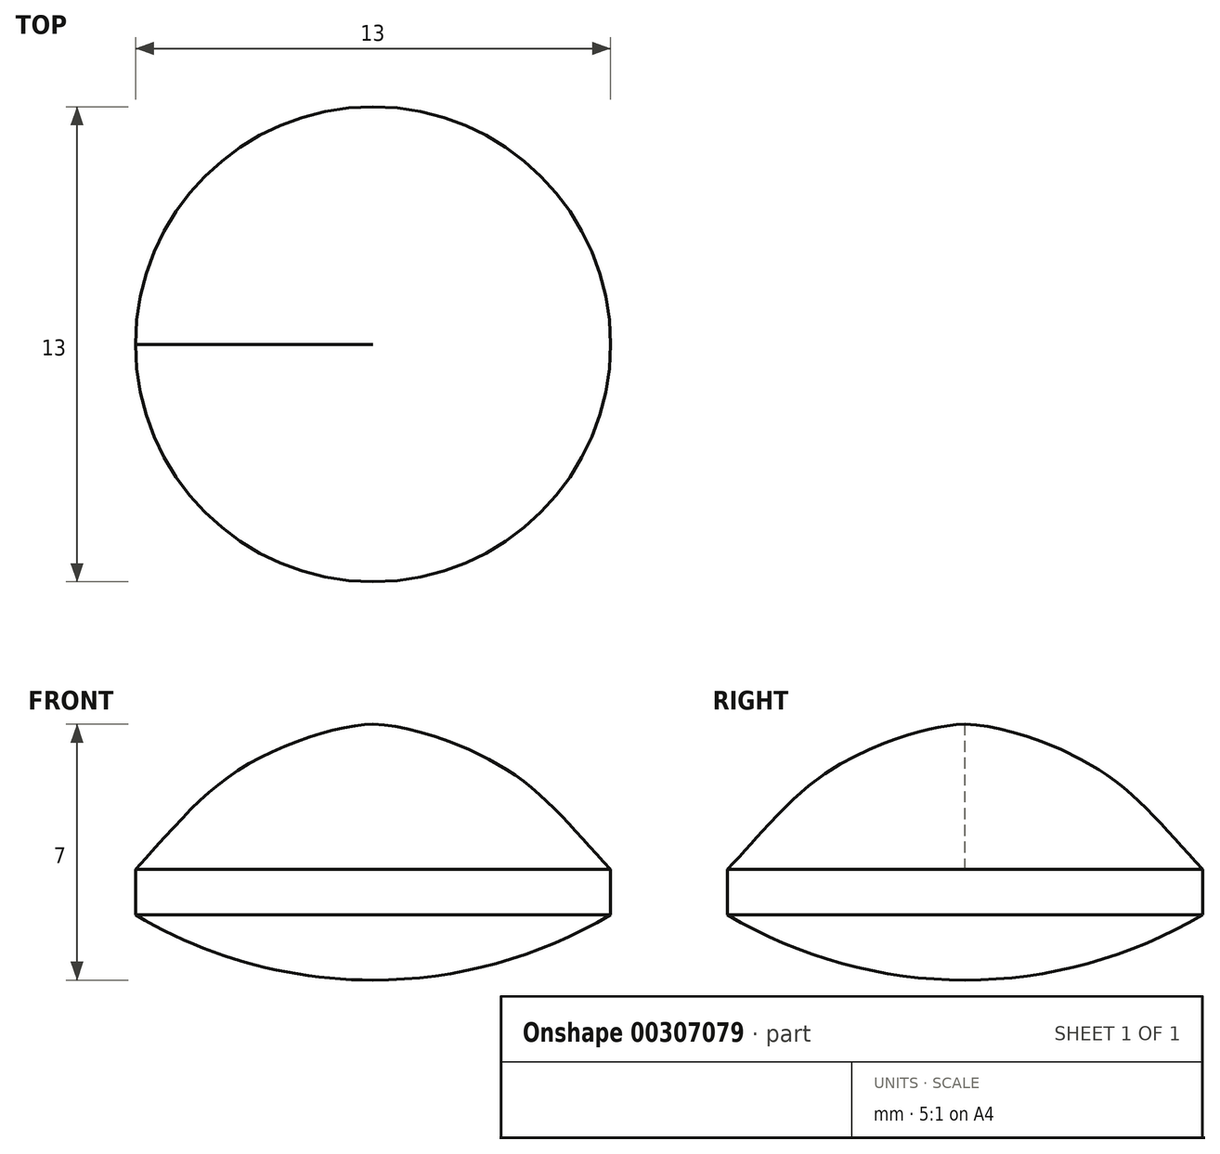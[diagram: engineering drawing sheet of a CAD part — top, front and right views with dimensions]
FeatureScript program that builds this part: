
annotation { "Feature Type Name" : "Feature", "Feature Type Description" : "" }
export const myFeature = defineFeature(function(context is Context, id is Id, definition is map)
    precondition{}
    {
        {
            var Q0;
            Q0=qCreatedBy(makeId("Front.planeOp"),FACE);
            var sketch = newSketch(context, id + "F0", { "sketchPlane" : qUnion([Q0])});
            skArc(sketch, "E0", {"start": v(-6.5, 1.79) * mm, "mid": v(-3.37, 0.45) * mm, "end": v(0, 0) * mm});
            skLineSegment(sketch, "E1", {"start": v(0, 23.83) * mm, "end": v(0, -8.8) * mm, "construction": true});
            skLineSegment(sketch, "E2", {"start": v(-6.5, 1.79) * mm, "end": v(-6.5, 3.03) * mm});
            skLineSegment(sketch, "E3", {"start": v(-6.5, 3.03) * mm, "end": v(0, 3.03) * mm});
            skFitSpline(sketch, "E4", {"points": [v(-6.5, 3.03) * mm, v(-3.4, 5.92) * mm, v(0, 7) * mm], "startDerivative": vector(6.57, 7.17) * mm, "endDerivative": vector(5.02, 0) * mm});
            skLineSegment(sketch, "E5", {"start": v(-6.5, 1.79) * mm, "end": v(0, 1.79) * mm});
            skArc(sketch, "E6", {"start": v(0, 7) * mm, "mid": v(-1.6, 6.34) * mm, "end": v(-2.27, 4.73) * mm, "construction": true});
            skLineSegment(sketch, "E7", {"start": v(0, 4.73) * mm, "end": v(-2.27, 4.73) * mm, "construction": true});
            skLineSegment(sketch, "E8", {"start": v(0, 7) * mm, "end": v(-1.08, 7) * mm, "construction": true});
            skLineSegment(sketch, "E9", {"start": v(0, 7) * mm, "end": v(0, 0) * mm});
            skSolve(sketch);
        }
        {
            var Q0;
            {var subQ0=sQuery(id+"F0.wireOp",EDGE,"E0");Q0=makeQuery(id+"F0.imprint","IMPRINT",FACE,{"disambiguationData":[TD([[makeQuery(id+"F0.imprint","IMPRINT",EDGE,{"derivedFrom":subQ0}),1.0]])]});}
            var Q1;
            Q1=makeQuery(id+"F0.imprint","IMPRINT",FACE,{"disambiguationData":[TD([[makeQuery(id+"F0.imprint","IMPRINT",EDGE,{"derivedFrom":sQuery(id+"F0.wireOp",EDGE,"E2")}),-1.0]])]});
            var Q2;
            {var subQ0=sQuery(id+"F0.wireOp",EDGE,"E3");Q2=makeQuery(id+"F0.imprint","IMPRINT",FACE,{"disambiguationData":[TD([[makeQuery(id+"F0.imprint","IMPRINT",EDGE,{"derivedFrom":subQ0}),1.0]])]});}
            var Q3;
            Q3=sQuery(id+"F0.wireOp",EDGE,"E9");
            revolve(context, id + "F1", {"entities" : qUnion([Q0, Q1, Q2]), "axis" : qUnion([Q3]), "revolveType" : RevolveType.FULL});
        }
    });
